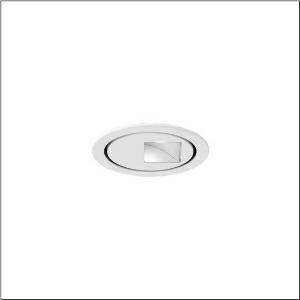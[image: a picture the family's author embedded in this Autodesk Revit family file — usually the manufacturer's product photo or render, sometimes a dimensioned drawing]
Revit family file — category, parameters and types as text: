
# Revit family: lunis_11_micro_round_51dj11b71wf21
name_source: partatom
category: Lighting Fixtures
units: mm (PartAtom-declared; Revit-internal decimal feet)

## family parameters
Cut with Voids When Loaded = No
Host = Face
Light Source = No
Part Type = Normal
Room Calculation Point = No
Round Connector Dimension = Use Diameter
Shared = No

## types (1)
- Lunis 11 micro round (1 x LED 3000K / CRI = 80 (unbekannt), 1320 lm, 3000K)
    Apparent Load = 20 VA
    CIE Flux Codes = 42 75 96 100 100
    Color Rendering = 80
    Color Temperature = 3000K
    Default Elevation = 1800 mm
    Description = Lunis 11 micro round, downlight, light control with wallwasher, of highly reflective aluminium, highly specular, light emission: direct distribution, LED rated luminous flux: 1.320lm, light colour: 830, with terminal, 3-pole, mains connection: 220..230V, AC, 50/60Hz, LED module, of aluminium, highly specular, white, diameter: 114mm, clamping range: 1..40mm, recessing ring, of plastic, traffic white (RAL 9016), protection rating (complete): IP20, insulation class (complete): insulation class II (safety insulation), certification: CE, permissible ambient temperature for indoor applications: 0..+35°C, packaging unit: 1 piece
    Height = 0 mm  [stored 0 ft]
    Lamp = 1 x LED 3000K / CRI >= 80 (unbekannt)
    Lamp Light Flux = 1320 lm
    Lamp count = 1
    Length = 114 mm
    Luminous efficacy = 67 lm/W
    Manufacturer = Siteco
    ModVariant = No
    Model = 51DJ11B71WF21
    Mounting Place = Ceiling
    Mounting Type = Recessed
    Number of Poles = 1
    OnlyDefault = Yes
    Power Factor = 1
    Product Name = Lunis 11 micro round
    Product group = downlight
    ProductGroupID = 401
    Protection Class = Protection class II
    Protection Degree = IP 20
    RLX_Detail_Level = 1
    RLX_Emergency_Light_Flux = 0 lm
    RLX_Emergency_Type = 0
    RLX_Emergency_Type_DB = No
    RlxData = <blob elided: 40553 chars, md5=85611ac8>
    Socket = socket
    Standby Power = 0 W
    System Light Flux = 1320 lm
    System Power = 20 W
    Type Comments = Product without accessories
    Type Image = l_1004773.jpg
    URL = http://relux.com
    VarID = ---
    Voltage = 0 V
    Weight = 0.00 kg
    Width = 114 mm

note: [stored X ft] marks values corroborated as IEEE doubles in the binary element streams (Revit-internal decimal feet)

## geometry (parser evidence)
native form markers: Blend x4, Sweep x10
no freeform markers — native parametric forms only
